# Revit family: ProxWay_Считыватель_карт_Mifare и меток Bluetooth LE_бескорпусный_PW-OEM MF BLE v2
name_source: partatom
category: Охранная сигнализация
units: mm (PartAtom-declared; Revit-internal decimal feet)

## family parameters
Всегда вертикально = Нет
На основе рабочей плоскости = Нет
Общий = Да
При загрузке вырезать с полостями = Нет
Размер круглого соединителя = Использовать диаметр
Сохранять ориентацию аннотаций = Нет
Тип детали = Нормальный
Точка расчета площади = Да

## types (1)
- PW-OEM-MF
    =Габариты= = =Габариты=
    ADSK_Единица измерения = шт.
    ADSK_Завод-изготовитель = ProxWay
    ADSK_Количество = 1
    ADSK_Марка = PW-OEM MF BLE v2
    ADSK_Материал = Зеленый
    ADSK_Наименование = Бескорпусный считыватель Mifare и меток Bluetooth LE (для скрытой установки в полости)
    ADSK_Напряжение = 12 В
    ADSK_Обозначение = RD
    ADSK_Раздел спецификации = 3. Периферийное оборудование
    ADSK_Размер_Высота = 55 мм
    ADSK_Размер_Глубина = 8 мм
    ADSK_Размер_Ширина = 26 мм
    ADSK_Тип = PW-OEM MF BLE v2
    ADSK_Ток дежурного режима = 50.000 мА
    ADSK_Ток тревожного режима = 50.000 мА
    URL = https://proxway-ble.ru
    Зона обслуживания_Отступ от прибора = 50 мм
    Отметка по умолчанию = 0 мм
    УГО_Тип = УГО_Считыватель
